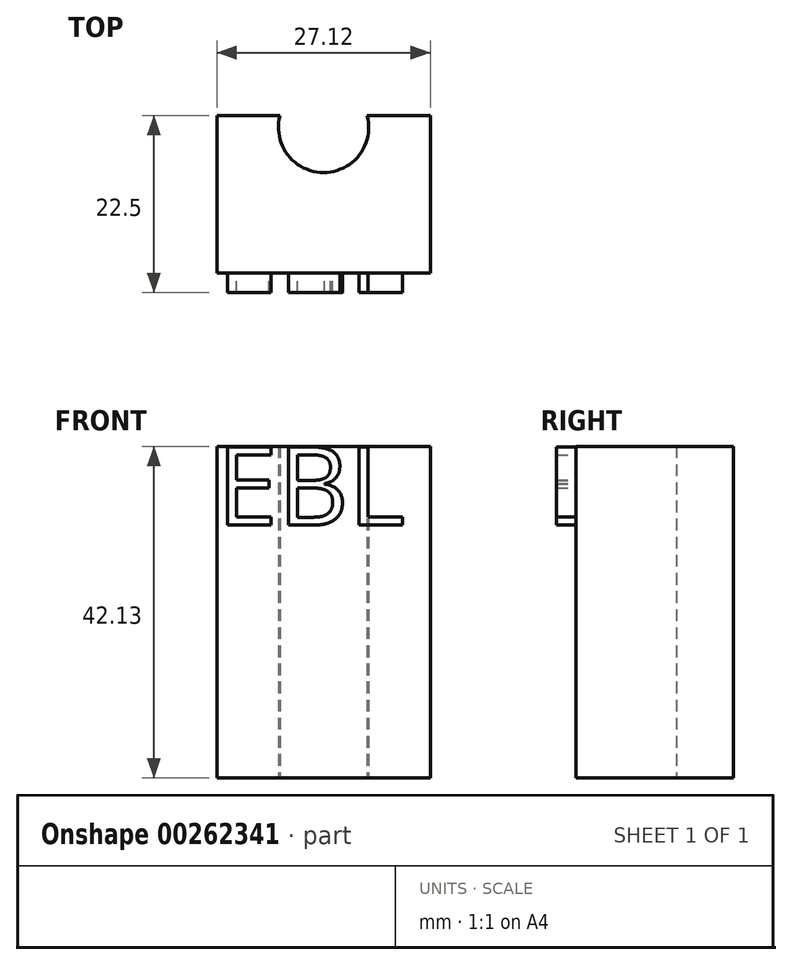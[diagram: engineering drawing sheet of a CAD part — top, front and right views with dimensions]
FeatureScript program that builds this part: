
annotation { "Feature Type Name" : "Feature", "Feature Type Description" : "" }
export const myFeature = defineFeature(function(context is Context, id is Id, definition is map)
    precondition{}
    {
        {
            var Q0;
            Q0=qCreatedBy(makeId("Top.planeOp"),FACE);
            var sketch = newSketch(context, id + "F0", { "sketchPlane" : qUnion([Q0])});
            skLineSegment(sketch, "E0.bottom", {"start": v(13.56, -10) * mm, "end": v(-13.56, -10) * mm});
            skLineSegment(sketch, "E0.top", {"start": v(13.56, 10) * mm, "end": v(-13.56, 10) * mm});
            skLineSegment(sketch, "E0.left", {"start": v(13.56, -10) * mm, "end": v(13.56, 10) * mm});
            skLineSegment(sketch, "E0.right", {"start": v(-13.56, -10) * mm, "end": v(-13.56, 10) * mm});
            skPoint(sketch, "E0.middle", {"position": v(0, 0) * mm});
            skCircle(sketch, "E1", {"center": v(0, 8.5) * mm, "radius": 5.72 * mm});
            skSolve(sketch);
        }
        {
            var Q0;
            Q0=makeQuery(id+"F0.imprint","IMPRINT",FACE,{"disambiguationData":[TD([[makeQuery(id+"F0.imprint","IMPRINT",EDGE,{"derivedFrom":sQuery(id+"F0.wireOp",EDGE,"E0.bottom")}),-1.0]])]});
            extrude(context, id + "F1", {"entities" : qUnion([Q0]), "depth" : 42.13 * mm});
        }
        {
            var Q0;
            Q0=makeQuery(id+"F1.opExtrude","SWEPT_FACE",FACE,{"disambiguationData":[OSD([sQuery(id+"F0.wireOp",EDGE,"E0.bottom")])]});
            var sketch = newSketch(context, id + "F2", { "sketchPlane" : qUnion([Q0])});
            skText(sketch, "E2", { "text": "EBL", "fontName": "OpenSans-Regular.ttf"});
            const initialGuessF2  = {"E2": [-0.01356, 0.03213, 1, 0, 0.01]};
            skSetInitialGuess(sketch, initialGuessF2);
            skSolve(sketch);
        }
        {
            var Q0;
            Q0 = qSketchRegion(id + "F2", true);
            extrude(context, id + "F3", {"entities" : qUnion([Q0]), "operationType" : NewBodyOperationType.ADD, "depth" : 2.5 * mm});
        }
    });
